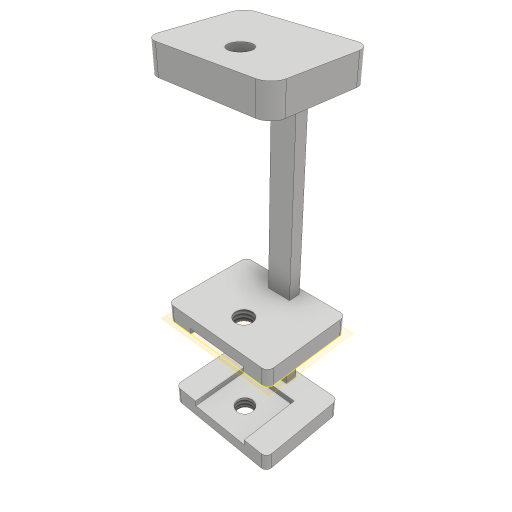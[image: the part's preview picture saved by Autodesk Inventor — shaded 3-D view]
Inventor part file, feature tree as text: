
AUTODESK INVENTOR PART (.ipt)
format: ipt  version: 2023 (Build 270158000, 158)  size: 212,480 bytes
history: native  units: mm
features: extrude x9, sketch x8, projected_geometry x5, fillet x2, plane x1, hole x1
ambient origin geometry x8: Origin, YZ Plane, XZ Plane, XY Plane, X Axis, Y Axis, Z Axis, Center Point
bodies: Solid1 (feature_tree)
feature tree (26):
  extrude  "Extrusion1"  Depth=15.0mm
  extrude  "Extrusion2"  Depth=2.0mm
  sketch  "Sketch6"  dims[d5=2.0mm d6=1.5mm d7=0.0mm]
  extrude  "Extrusion5"  Depth=2.0mm TaperAngle=0.0deg
  extrude  "Extrusion6"  Depth=1.0mm TaperAngle=0.0deg
  fillet  "Fillet2"  Radius=4.0mm
  fillet  "Fillet3"  Radius=1.0mm
  extrude  "Extrusion10"  Depth=10.0mm TaperAngle=0.0deg
  extrude  "Extrusion12"  Depth=10.2mm
  plane  "Work Plane1"
  sketch  "Sketch14"  dims[d67=10.2mm d68=10.2mm]
  extrude  "Extrusion13"  Depth=1.0mm TaperAngle=0.0deg
  hole  "Hole1"  [1 undecoded]
  extrude  "Extrusion14"  Depth=1.0mm TaperAngle=0.0deg
  extrude  "Extrusion15"  Depth=1.0mm TaperAngle=0.0deg
  sketch  "Sketch1"  dims[d0=19.0mm d1=15.0mm]
  sketch  "Sketch2"  dims[d2=3.0mm d3=0.0mm d4=2.0mm]
  sketch  "Sketch7"  dims[d13=4.0mm d14=47.0mm d15=0.0mm d16=4.0mm d17=0.0mm d47=1.0mm]
  projected_geometry  "Projected Loop2"
  sketch  "Sketch13"  dims[d48=2.0mm d55=10.0mm d56=0.0mm]
  projected_geometry  "Projected Loop4"
  projected_geometry  "Projected Loop5"
  projected_geometry  "Projected Loop6"
  sketch  "Sketch15"  dims[d69=4.5mm d70=1.0mm d71=0.0mm]
  projected_geometry  "Projected Loop7"
  sketch  "Sketch16"  dims[d72=13.0mm d73=3.0mm d74=0.0mm d75=3.242mm d76=25.0mm d77=9.4mm d78=2.0mm d79=90.0deg d80=8.0mm d81=20.594885mm d82=1.0mm d83=0.0mm d84=1.0mm d85=0.0mm]
note: 1 required parameter value undecoded (feature->parameter linkage not recoverable at this tier; creation-order binding heuristic only, values carry confidence <= 0.55)
